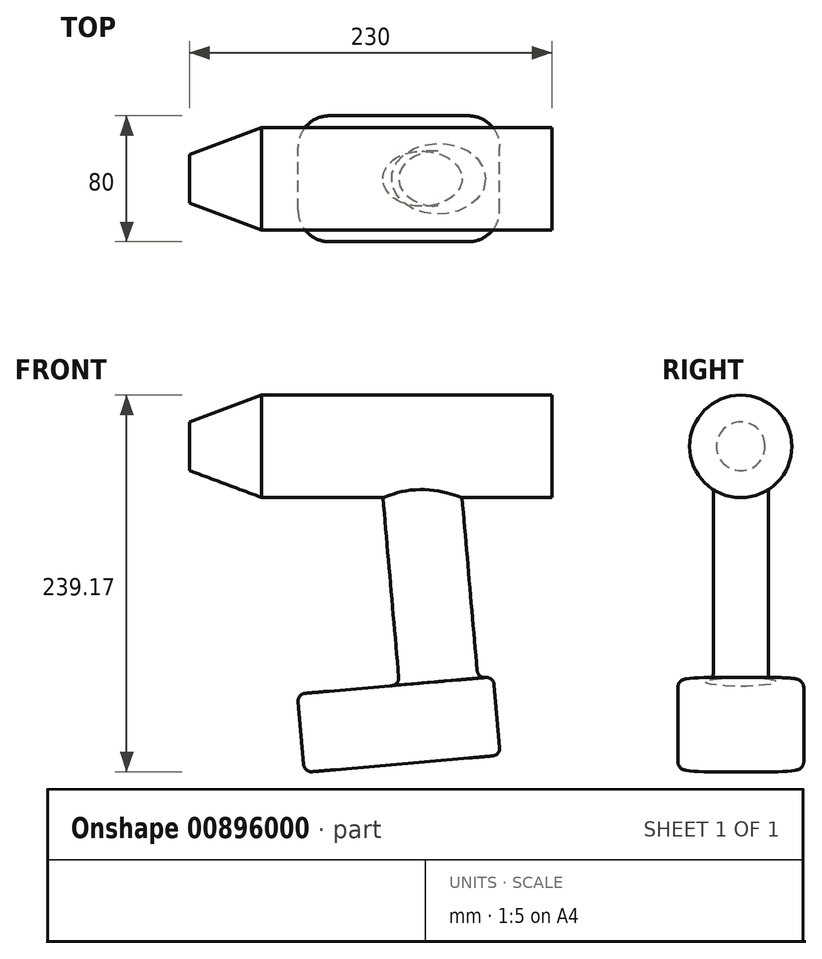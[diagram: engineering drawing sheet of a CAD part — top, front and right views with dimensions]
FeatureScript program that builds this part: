
annotation { "Feature Type Name" : "Feature", "Feature Type Description" : "" }
export const myFeature = defineFeature(function(context is Context, id is Id, definition is map)
    precondition{}
    {
        {
            var Q0;
            Q0=qCreatedBy(makeId("Right.planeOp"),FACE);
            var sketch = newSketch(context, id + "F0", { "sketchPlane" : qUnion([Q0])});
            skCircle(sketch, "E0", {"center": v(0, 0) * mm, "radius": 32.5 * mm});
            skSolve(sketch);
        }
        {
            var Q0;
            Q0=makeQuery(id+"F0.imprint","IMPRINT",FACE,{"disambiguationData":[TD([[makeQuery(id+"F0.imprint","IMPRINT",EDGE,{"derivedFrom":sQuery(id+"F0.wireOp",EDGE,"E0")}),1.0]])]});
            extrude(context, id + "F1", {"entities" : qUnion([Q0]), "depth" : 85 * mm, "offsetDistance" : 25.4 * mm, "hasSecondDirection" : true, "secondDirectionOppositeDirection" : true, "secondDirectionDepth" : 145 * mm});
        }
        {
            var Q0;
            Q0=qCreatedBy(makeId("Top.planeOp"),FACE);
            var sketch = newSketch(context, id + "F2", { "sketchPlane" : qUnion([Q0])});
            skLineSegment(sketch, "E1", {"start": v(0, 49.9) * mm, "end": v(0, -54.3) * mm, "construction": true});
            skSolve(sketch);
        }
        {
            var Q0;
            Q0=sQuery(id+"F2.wireOp",EDGE,"E1");
            var Q1;
            Q1=qCreatedBy(makeId("Top.planeOp"),FACE);
            cPlane(context, id + "F3", {"entities" : qUnion([Q0, Q1]), "cplaneType" : CPlaneType.LINE_ANGLE, "offset" : 25.4 * mm, "angle" : 5 * degree, "width" : 152.4 * mm, "height" : 152.4 * mm});
        }
        {
            var Q0;
            Q0=qCreatedBy(id+"F3.planeOp",FACE);
            var sketch = newSketch(context, id + "F4", { "sketchPlane" : qUnion([Q0])});
            skEllipse(sketch, "E2", {"center": v(0, 0) * mm, "majorRadius": 25 * mm, "minorRadius": 17.5 * mm, "majorAxis": v(1, 0)});
            skSolve(sketch);
        }
        {
            var Q0;
            Q0 = qSketchRegion(id + "F4", true);
            extrude(context, id + "F5", {"entities" : qUnion([Q0]), "operationType" : NewBodyOperationType.ADD, "depth" : 150 * mm, "offsetDistance" : 25.4 * mm});
        }
        {
            var Q0;
            Q0=makeQuery(id+"F5.opExtrude","CAP_FACE",FACE,{"disambiguationData":[OSD([sQuery(id+"F4.wireOp",EDGE,"E2")])],"isStart":false});
            cPlane(context, id + "F6", {"entities" : qUnion([Q0]), "cplaneType" : CPlaneType.OFFSET, "offset" : 0 * mm, "oppositeDirection" : true, "width" : 152.4 * mm, "height" : 152.4 * mm});
        }
        {
            var Q0;
            Q0=qCreatedBy(id+"F6.planeOp",FACE);
            var sketch = newSketch(context, id + "F7", { "sketchPlane" : qUnion([Q0])});
            skPoint(sketch, "E3", {"position": v(0, 0) * mm});
            skLineSegment(sketch, "E4.bottom", {"start": v(35, 40) * mm, "end": v(-90, 40) * mm});
            skLineSegment(sketch, "E4.top", {"start": v(35, -40) * mm, "end": v(-90, -40) * mm});
            skLineSegment(sketch, "E4.left", {"start": v(35, 40) * mm, "end": v(35, -40) * mm});
            skLineSegment(sketch, "E4.right", {"start": v(-90, 40) * mm, "end": v(-90, -40) * mm});
            skLineSegment(sketch, "E5", {"start": v(0, 97.32) * mm, "end": v(0, -100.26) * mm, "construction": true});
            skLineSegment(sketch, "E6", {"start": v(103.8, 0) * mm, "end": v(-154.14, 0) * mm, "construction": true});
            skSolve(sketch);
        }
        {
            var Q0;
            Q0=makeQuery(id+"F7.imprint","IMPRINT",FACE,{"disambiguationData":[TD([[makeQuery(id+"F7.imprint","IMPRINT",EDGE,{"derivedFrom":sQuery(id+"F7.wireOp",EDGE,"E4.bottom")}),1.0]])]});
            extrude(context, id + "F8", {"entities" : qUnion([Q0]), "operationType" : NewBodyOperationType.ADD, "depth" : 50 * mm, "offsetDistance" : 25.4 * mm});
        }
        {
            var Q0;
            Q0=qCreatedBy(makeId("Front.planeOp"),FACE);
            var sketch = newSketch(context, id + "F9", { "sketchPlane" : qUnion([Q0])});
            skLineSegment(sketch, "E7", {"start": v(-145, 15.47) * mm, "end": v(-99.3, 32.5) * mm});
            skLineSegment(sketch, "E8", {"start": v(-145, 15.47) * mm, "end": v(-145, 32.5) * mm});
            skLineSegment(sketch, "E9", {"start": v(-99.3, 32.5) * mm, "end": v(-145, 32.5) * mm});
            skLineSegment(sketch, "E10", {"start": v(-216.27, 0) * mm, "end": v(81.4, 0) * mm, "construction": true});
            skSolve(sketch);
        }
        {
            var Q0;
            Q0 = qSketchRegion(id + "F9", true);
            var Q1;
            Q1=sQuery(id+"F9.wireOp",EDGE,"E10");
            revolve(context, id + "F10", {"operationType" : NewBodyOperationType.REMOVE, "surfaceOperationType" : NewSurfaceOperationType.NEW, "entities" : qUnion([Q0]), "axis" : qUnion([Q1]), "revolveType" : RevolveType.FULL, "oppositeDirection" : true});
        }
        {
            var Q0;
            Q0=makeQuery(id+"F8.opExtrude","SWEPT_EDGE",EDGE,{"disambiguationData":[OSD([sQuery(id+"F7.wireOp",EDGE,"E4.top"),sQuery(id+"F7.wireOp",EDGE,"E4.right")])]});
            var Q1;
            Q1=makeQuery(id+"F8.opExtrude","SWEPT_EDGE",EDGE,{"disambiguationData":[OSD([sQuery(id+"F7.wireOp",EDGE,"E4.bottom"),sQuery(id+"F7.wireOp",EDGE,"E4.right")])]});
            var Q2;
            Q2=makeQuery(id+"F8.opExtrude","SWEPT_EDGE",EDGE,{"disambiguationData":[OSD([sQuery(id+"F7.wireOp",EDGE,"E4.bottom"),sQuery(id+"F7.wireOp",EDGE,"E4.left")])]});
            var Q3;
            Q3=makeQuery(id+"F8.opExtrude","SWEPT_EDGE",EDGE,{"disambiguationData":[OSD([sQuery(id+"F7.wireOp",EDGE,"E4.top"),sQuery(id+"F7.wireOp",EDGE,"E4.left")])]});
            fillet(context, id + "F11", {"entities" : qUnion([Q0, Q1, Q2, Q3]), "radius" : 20 * mm, "tangentPropagation" : true, "allowEdgeOverflow" : false});
        }
        {
            var Q0;
            Q0=makeQuery(id+"F5.opExtrude","CAP_EDGE",EDGE,{"disambiguationData":[OSD([sQuery(id+"F4.wireOp",EDGE,"E2")])],"isStart":false});
            var Q1;
            Q1=makeQuery(id+"F8.opExtrude","CAP_FACE",FACE,{"disambiguationData":[OSD([sQuery(id+"F7.wireOp",EDGE,"E4.bottom"),sQuery(id+"F7.wireOp",EDGE,"E4.top"),sQuery(id+"F7.wireOp",EDGE,"E4.left"),sQuery(id+"F7.wireOp",EDGE,"E4.right")])],"isStart":true});
            var Q2;
            Q2=makeQuery(id+"F8.opExtrude","CAP_FACE",FACE,{"disambiguationData":[OSD([sQuery(id+"F7.wireOp",EDGE,"E4.bottom"),sQuery(id+"F7.wireOp",EDGE,"E4.top"),sQuery(id+"F7.wireOp",EDGE,"E4.left"),sQuery(id+"F7.wireOp",EDGE,"E4.right")])],"isStart":false});
            fillet(context, id + "F12", {"entities" : qUnion([Q0, Q1, Q2]), "radius" : 5 * mm, "tangentPropagation" : true, "allowEdgeOverflow" : false});
        }
    });
